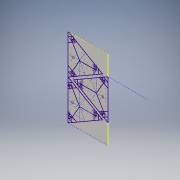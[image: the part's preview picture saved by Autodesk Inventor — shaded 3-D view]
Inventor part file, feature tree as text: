
AUTODESK INVENTOR PART (.ipt)
format: ipt  version: 2016 (Build 200138000, 138)  size: 384,512 bytes
history: native  units: in
note: dims shown in document units (in); Inventor stores cm internally (conversion verified against a paired STEP export)
features: hole x6, sketch x1, extrude x1, other x1
ambient origin geometry x8: Origin, YZ Plane, XZ Plane, XY Plane, X Axis, Y Axis, Z Axis, Center Point
bodies: Solid1 (feature_tree)
feature tree (9):
  sketch  "Sketch1"  dims[d2=0.063in d3=0.0in d4=24.0in d5=12.0in d7=30.0deg d9=60.0deg d11=30.0deg d20=60.0deg d27=12.0in d28=150.0deg d29=12.0in d30=60.0deg d31=3.0in d32=3.0in d33=3.0in d34=3.0in d35=3.0in d36=3.0in d38=3.0in d39=3.0in d40=3.0in d41=0.9055in d42=2.2835in d43=0.9055in d44=2.2835in d45=0.9055in d46=2.2835in d47=1.9291in d48=2.2835in d49=1.9291in d50=2.2835in d51=1.9291in d52=2.2835in d53=1.4173in d54=1.4173in d55=1.4173in d56=1.4173in d57=1.4173in d58=1.4173in d61=0.9449in d62=1.2205in d63=0.9449in d64=1.2205in d65=0.9449in d66=1.2205in d74=0.0984in d75=0.75in d76=0.375in d77=0.25in d78=0.5635in d79=1.0in d80=0.8108in d81=0.6772in d82=6.0743in d83=0.6772in d84=0.6772in d85=0.6772in d86=0.6772in d87=0.6772in d88=0.6772in d89=0.6772in d90=0.6772in d91=1.5in d92=0.0984in d93=0.75in d94=0.375in d95=0.25in d96=0.5635in d97=1.0in d98=0.8108in d99=0.7087in d100=0.75in d101=0.375in d102=0.25in d103=0.5635in d104=1.0in d105=0.8108in d106=1.4173in d107=1.4173in d108=1.4173in d109=1.4173in d110=1.4173in d111=1.4173in d112=1.4173in d113=1.4173in d114=1.4173in d115=1.4173in d116=1.4173in d117=1.4173in d118=1.5in d119=1.5in d120=1.5in d121=1.5in d122=1.5in d123=1.5in d124=1.5in d125=1.5in d155=0.8268in d157=0.3543in d158=0.8268in d159=0.3543in d160=0.8268in d164=0.3543in d165=0.8268in d166=0.3543in d167=0.8268in d168=0.3543in d169=0.8268in d170=0.3543in d171=0.8268in d172=0.3543in d173=0.8268in d174=0.3543in d175=0.8268in d176=0.3543in d177=0.6693in d178=0.75in d179=0.375in d180=0.25in d181=0.5635in d182=1.0in d183=0.8108in d184=0.0984in d185=0.75in d186=0.375in d187=0.25in d188=0.5635in d189=1.0in d190=0.8108in d214=150.0deg d215=4.9in d216=30.0deg d217=4.9in d218=4.9in d219=90.0deg d220=4.9in d221=4.9in d222=4.9in d224=30.0deg d225=150.0deg d226=90.0deg d227=4.9in d228=4.9in d229=4.9in d231=30.0deg d232=150.0deg d233=90.0deg d191=1.0in d192=1.0in]
  extrude  "Extrusion1"  Depth=24.0in
  other  "3 frames"
  hole  "Holes"  [1 undecoded]
  hole  "Top Mount Holes"  [1 undecoded]
  hole  "Wire-through Holes"  [1 undecoded]
  hole  "Motor Mount Holes"  [1 undecoded]
  hole  "Motor Axle Holes"  [1 undecoded]
  hole  "Motor Pro. Holes"  [1 undecoded]
note: 6 required parameter values undecoded (feature->parameter linkage not recoverable at this tier; creation-order binding heuristic only, values carry confidence <= 0.55)
